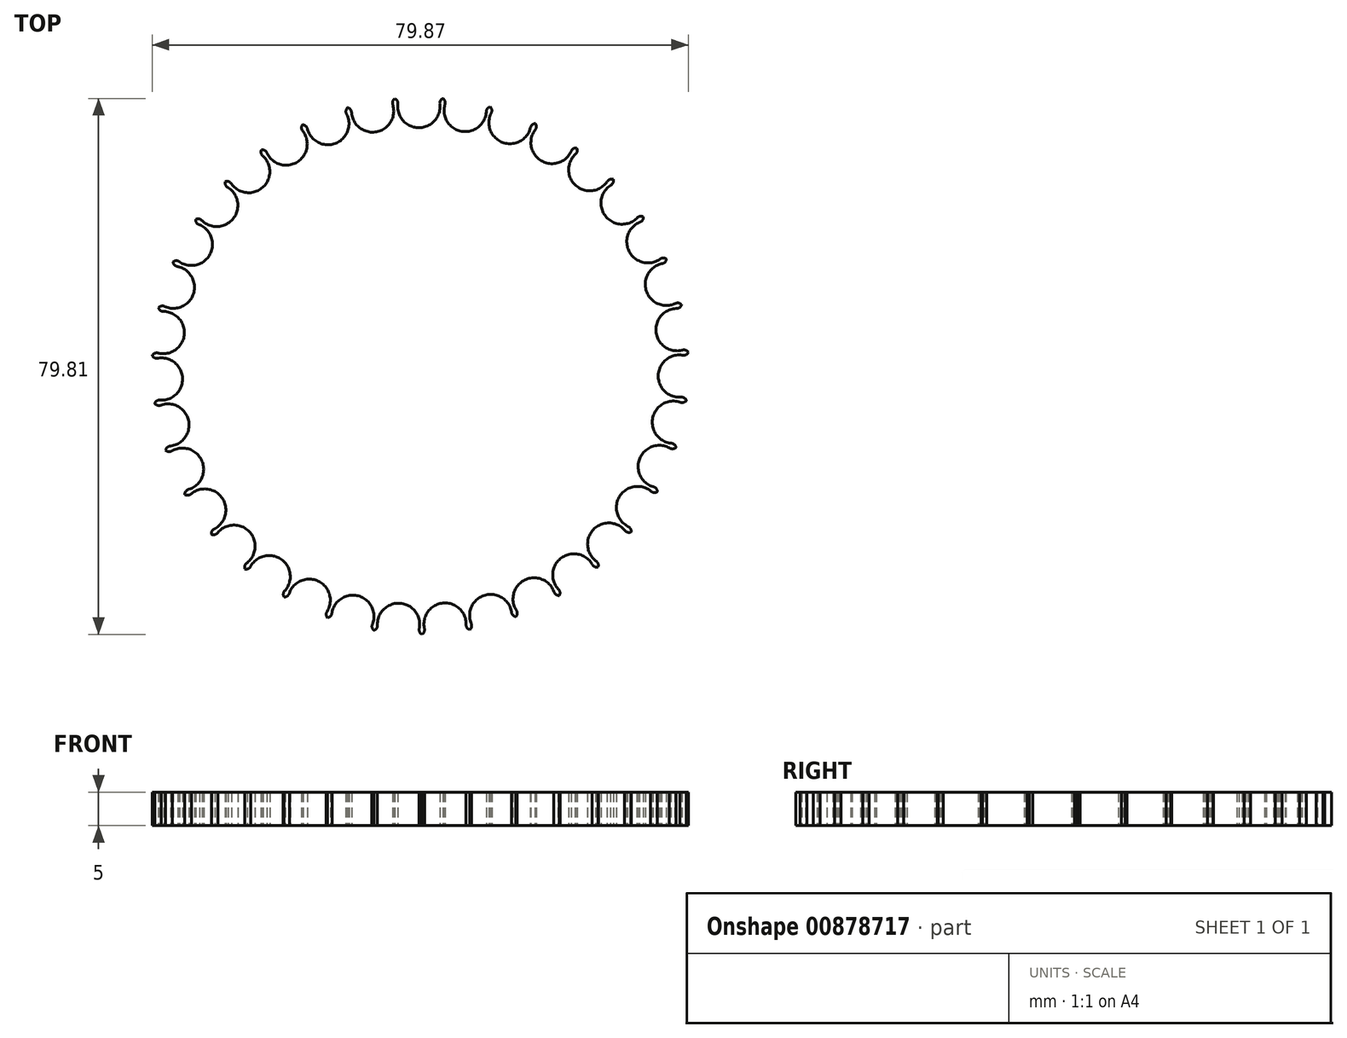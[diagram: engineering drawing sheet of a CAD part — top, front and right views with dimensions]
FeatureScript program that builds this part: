
annotation { "Feature Type Name" : "Feature", "Feature Type Description" : "" }
export const myFeature = defineFeature(function(context is Context, id is Id, definition is map)
    precondition{}
    {
        {
            var Q0;
            Q0=qCreatedBy(makeId("Top.planeOp"),FACE);
            var sketch = newSketch(context, id + "F0", { "sketchPlane" : qUnion([Q0])});
            skArc(sketch, "E0.0", {"start": v(-27.46, 84.28) * mm, "mid": v(-28.98, 79.88) * mm, "end": v(-24.46, 78.78) * mm});
            skArc(sketch, "E1.0", {"start": v(-31.8, 89.77) * mm, "mid": v(-32.52, 85.17) * mm, "end": v(-27.87, 84.9) * mm});
            skArc(sketch, "E2.0", {"start": v(-24.17, 78.1) * mm, "mid": v(-26.45, 74.05) * mm, "end": v(-22.2, 72.16) * mm});
            skArc(sketch, "E3.0", {"start": v(-22.03, 71.44) * mm, "mid": v(-25, 67.86) * mm, "end": v(-21.15, 65.23) * mm});
            skArc(sketch, "E4.0", {"start": v(-21.11, 64.5) * mm, "mid": v(-24.68, 61.5) * mm, "end": v(-21.36, 58.24) * mm});
            skArc(sketch, "E5.0", {"start": v(-21.45, 57.5) * mm, "mid": v(-25.5, 55.2) * mm, "end": v(-22.81, 51.39) * mm});
            skArc(sketch, "E6.0", {"start": v(-23.04, 50.7) * mm, "mid": v(-27.42, 49.14) * mm, "end": v(-25.47, 44.91) * mm});
            skArc(sketch, "E7.0", {"start": v(-25.81, 44.26) * mm, "mid": v(-30.4, 43.52) * mm, "end": v(-29.24, 39.01) * mm});
            skArc(sketch, "E8.0.0", {"start": v(-24.46, 78.78) * mm, "mid": v(-28.98, 79.88) * mm, "end": v(-27.46, 84.28) * mm});
            skArc(sketch, "E8.0.1", {"start": v(-27.46, 84.28) * mm, "mid": v(-27.01, 84.61) * mm, "end": v(-26.9, 85.16) * mm});
            skArc(sketch, "E8.0.3", {"start": v(-23.42, 78.78) * mm, "mid": v(-23.94, 78.98) * mm, "end": v(-24.46, 78.78) * mm});
            skArc(sketch, "E9.0", {"start": v(-29.69, 38.44) * mm, "mid": v(-34.34, 38.52) * mm, "end": v(-34, 33.88) * mm});
            skArc(sketch, "E10.0", {"start": v(-34.55, 33.4) * mm, "mid": v(-39.11, 34.31) * mm, "end": v(-39.6, 29.68) * mm});
            skArc(sketch, "E11.0", {"start": v(-40.22, 29.3) * mm, "mid": v(-44.55, 31.02) * mm, "end": v(-45.86, 26.55) * mm});
            skArc(sketch, "E12.0", {"start": v(-46.54, 26.29) * mm, "mid": v(-50.5, 28.75) * mm, "end": v(-52.58, 24.58) * mm});
            skArc(sketch, "E13.0", {"start": v(-53.3, 24.45) * mm, "mid": v(-56.75, 27.58) * mm, "end": v(-59.54, 23.85) * mm});
            skArc(sketch, "E14.0", {"start": v(-60.27, 23.85) * mm, "mid": v(-63.1, 27.54) * mm, "end": v(-66.52, 24.37) * mm});
            skArc(sketch, "E15.0", {"start": v(-67.24, 24.5) * mm, "mid": v(-69.37, 28.64) * mm, "end": v(-73.3, 26.13) * mm});
            skArc(sketch, "E16.0", {"start": v(-73.98, 26.39) * mm, "mid": v(-75.34, 30.84) * mm, "end": v(-79.65, 29.08) * mm});
            skArc(sketch, "E17.0", {"start": v(-80.28, 29.45) * mm, "mid": v(-80.82, 34.07) * mm, "end": v(-85.37, 33.1) * mm});
            skArc(sketch, "E18.0", {"start": v(-85.93, 33.58) * mm, "mid": v(-85.63, 38.23) * mm, "end": v(-90.29, 38.1) * mm});
            skArc(sketch, "E19.0", {"start": v(-90.75, 38.66) * mm, "mid": v(-89.63, 43.18) * mm, "end": v(-94.23, 43.87) * mm});
            skArc(sketch, "E20.0", {"start": v(-94.58, 44.52) * mm, "mid": v(-92.67, 48.76) * mm, "end": v(-97.08, 50.27) * mm});
            skArc(sketch, "E21.0", {"start": v(-97.3, 50.97) * mm, "mid": v(-94.67, 54.8) * mm, "end": v(-98.74, 57.07) * mm});
            skArc(sketch, "E22.0", {"start": v(-98.84, 57.8) * mm, "mid": v(-95.56, 61.1) * mm, "end": v(-99.16, 64.06) * mm});
            skArc(sketch, "E23.0", {"start": v(-99.13, 64.8) * mm, "mid": v(-95.31, 67.46) * mm, "end": v(-98.32, 71) * mm});
            skArc(sketch, "E24.0", {"start": v(-98.16, 71.72) * mm, "mid": v(-93.93, 73.67) * mm, "end": v(-96.26, 77.7) * mm});
            skArc(sketch, "E25.0", {"start": v(-95.98, 78.37) * mm, "mid": v(-91.46, 79.53) * mm, "end": v(-93.04, 83.91) * mm});
            skArc(sketch, "E26.0", {"start": v(-92.64, 84.53) * mm, "mid": v(-88, 84.86) * mm, "end": v(-88.75, 89.45) * mm});
            skArc(sketch, "E27.0", {"start": v(-88.25, 89.98) * mm, "mid": v(-83.62, 89.48) * mm, "end": v(-83.55, 94.13) * mm});
            skArc(sketch, "E28.0", {"start": v(-82.96, 94.57) * mm, "mid": v(-78.5, 93.25) * mm, "end": v(-77.6, 97.82) * mm});
            skArc(sketch, "E29.0", {"start": v(-76.94, 98.14) * mm, "mid": v(-72.78, 96.04) * mm, "end": v(-71.08, 100.37) * mm});
            skArc(sketch, "E30.0", {"start": v(-70.38, 100.57) * mm, "mid": v(-66.66, 97.77) * mm, "end": v(-64.21, 101.73) * mm});
            skPoint(sketch, "E31.0", {"position": v(-60.33, 98.37) * mm});
            skArc(sketch, "E32.0", {"start": v(-63.48, 101.8) * mm, "mid": v(-60.33, 98.37) * mm, "end": v(-57.21, 101.83) * mm});
            skArc(sketch, "E33.0", {"start": v(-56.48, 101.77) * mm, "mid": v(-54, 97.84) * mm, "end": v(-50.3, 100.69) * mm});
            skArc(sketch, "E34.0", {"start": v(-49.6, 100.5) * mm, "mid": v(-47.85, 96.18) * mm, "end": v(-43.72, 98.33) * mm});
            skArc(sketch, "E35.0", {"start": v(-43.06, 98.01) * mm, "mid": v(-42.1, 93.45) * mm, "end": v(-37.65, 94.83) * mm});
            skArc(sketch, "E36.0", {"start": v(-37.06, 94.4) * mm, "mid": v(-36.94, 89.74) * mm, "end": v(-32.31, 90.3) * mm});
            skPoint(sketch, "E37.0", {"position": v(-31.42, 90.18) * mm});
            skArc(sketch, "E38.0", {"start": v(-31.8, 89.77) * mm, "mid": v(-31.42, 90.18) * mm, "end": v(-31.4, 90.73) * mm});
            skArc(sketch, "E39.0", {"start": v(-32.31, 90.3) * mm, "mid": v(-31.9, 90.67) * mm, "end": v(-31.34, 90.67) * mm});
            skArc(sketch, "E40.0", {"start": v(-27.87, 84.9) * mm, "mid": v(-27.4, 85.18) * mm, "end": v(-26.84, 85.08) * mm});
            skArc(sketch, "E41.0", {"start": v(-24.17, 78.1) * mm, "mid": v(-23.67, 78.35) * mm, "end": v(-23.45, 78.87) * mm});
            skPoint(sketch, "E42.0", {"position": v(-21.65, 72.26) * mm});
            skArc(sketch, "E43.0", {"start": v(-22.2, 72.16) * mm, "mid": v(-21.65, 72.26) * mm, "end": v(-21.17, 71.97) * mm});
            skArc(sketch, "E44.0", {"start": v(-22.03, 71.44) * mm, "mid": v(-21.5, 71.6) * mm, "end": v(-21.2, 72.06) * mm});
            skPoint(sketch, "E45.0", {"position": v(-20.6, 65.24) * mm});
            skArc(sketch, "E46.0", {"start": v(-21.15, 65.23) * mm, "mid": v(-20.6, 65.24) * mm, "end": v(-20.18, 64.87) * mm});
            skArc(sketch, "E47.0", {"start": v(-21.11, 64.5) * mm, "mid": v(-20.56, 64.55) * mm, "end": v(-20.18, 64.96) * mm});
            skArc(sketch, "E48.0", {"start": v(-21.36, 58.24) * mm, "mid": v(-20.81, 58.14) * mm, "end": v(-20.47, 57.7) * mm});
            skArc(sketch, "E49.0", {"start": v(-21.45, 57.5) * mm, "mid": v(-20.9, 57.46) * mm, "end": v(-20.45, 57.8) * mm});
            skPoint(sketch, "E50.0", {"position": v(-22.3, 51.2) * mm});
            skArc(sketch, "E51.0", {"start": v(-22.81, 51.39) * mm, "mid": v(-22.3, 51.2) * mm, "end": v(-22.03, 50.7) * mm});
            skArc(sketch, "E52.0", {"start": v(-23.04, 50.7) * mm, "mid": v(-22.5, 50.54) * mm, "end": v(-22, 50.8) * mm});
            skArc(sketch, "E53.0", {"start": v(-25.47, 44.91) * mm, "mid": v(-24.99, 44.63) * mm, "end": v(-24.82, 44.1) * mm});
            skPoint(sketch, "E54.0", {"position": v(-25.3, 44.03) * mm});
            skArc(sketch, "E55.0", {"start": v(-25.81, 44.26) * mm, "mid": v(-25.3, 44.02) * mm, "end": v(-24.77, 44.18) * mm});
            skPoint(sketch, "E56.0", {"position": v(-28.82, 38.65) * mm});
            skArc(sketch, "E57.0", {"start": v(-29.24, 39.01) * mm, "mid": v(-28.81, 38.65) * mm, "end": v(-28.74, 38.1) * mm});
            skArc(sketch, "E58.0", {"start": v(-29.69, 38.44) * mm, "mid": v(-29.24, 38.11) * mm, "end": v(-28.68, 38.17) * mm});
            skArc(sketch, "E59.0", {"start": v(-34, 33.88) * mm, "mid": v(-33.65, 33.45) * mm, "end": v(-33.67, 32.9) * mm});
            skArc(sketch, "E60.0", {"start": v(-34.55, 33.4) * mm, "mid": v(-34.16, 33) * mm, "end": v(-33.6, 32.95) * mm});
            skPoint(sketch, "E61.0", {"position": v(-39.33, 29.2) * mm});
            skArc(sketch, "E62.0", {"start": v(-39.6, 29.68) * mm, "mid": v(-39.33, 29.2) * mm, "end": v(-39.46, 28.65) * mm});
            skPoint(sketch, "E63.0", {"position": v(-39.91, 28.84) * mm});
            skArc(sketch, "E64.0", {"start": v(-40.22, 29.3) * mm, "mid": v(-39.92, 28.84) * mm, "end": v(-39.38, 28.7) * mm});
            skArc(sketch, "E65.0", {"start": v(-45.86, 26.55) * mm, "mid": v(-45.68, 26.02) * mm, "end": v(-45.9, 25.5) * mm});
            skArc(sketch, "E66.0", {"start": v(-46.54, 26.29) * mm, "mid": v(-46.32, 25.78) * mm, "end": v(-45.82, 25.54) * mm});
            skArc(sketch, "E67.0", {"start": v(-52.58, 24.58) * mm, "mid": v(-52.5, 24.03) * mm, "end": v(-52.8, 23.57) * mm});
            skPoint(sketch, "E68.0", {"position": v(-53.17, 23.9) * mm});
            skArc(sketch, "E69.0", {"start": v(-53.3, 24.45) * mm, "mid": v(-53.17, 23.9) * mm, "end": v(-52.72, 23.59) * mm});
            skPoint(sketch, "E70.0", {"position": v(-59.56, 23.3) * mm});
            skArc(sketch, "E71.0", {"start": v(-59.54, 23.85) * mm, "mid": v(-59.56, 23.3) * mm, "end": v(-59.95, 22.9) * mm});
            skPoint(sketch, "E72.0", {"position": v(-60.24, 23.3) * mm});
            skArc(sketch, "E73.0", {"start": v(-60.27, 23.85) * mm, "mid": v(-60.24, 23.3) * mm, "end": v(-59.85, 22.9) * mm});
            skArc(sketch, "E74.0", {"start": v(-66.52, 24.37) * mm, "mid": v(-66.64, 23.83) * mm, "end": v(-67.1, 23.5) * mm});
            skArc(sketch, "E75.0", {"start": v(-67.24, 24.5) * mm, "mid": v(-67.31, 23.95) * mm, "end": v(-67, 23.49) * mm});
            skPoint(sketch, "E76.0", {"position": v(-73.51, 25.62) * mm});
            skArc(sketch, "E77.0", {"start": v(-73.3, 26.13) * mm, "mid": v(-73.5, 25.62) * mm, "end": v(-74.01, 25.38) * mm});
            skArc(sketch, "E78.0", {"start": v(-73.98, 26.39) * mm, "mid": v(-74.15, 25.86) * mm, "end": v(-73.93, 25.35) * mm});
            skPoint(sketch, "E79.0", {"position": v(-79.95, 28.61) * mm});
            skArc(sketch, "E80.0", {"start": v(-79.65, 29.08) * mm, "mid": v(-79.95, 28.6) * mm, "end": v(-80.49, 28.46) * mm});
            skArc(sketch, "E81.0", {"start": v(-80.28, 29.45) * mm, "mid": v(-80.54, 28.96) * mm, "end": v(-80.4, 28.42) * mm});
            skArc(sketch, "E82.0", {"start": v(-85.37, 33.1) * mm, "mid": v(-85.75, 32.7) * mm, "end": v(-86.3, 32.65) * mm});
            skArc(sketch, "E83.0", {"start": v(-85.93, 33.58) * mm, "mid": v(-86.27, 33.15) * mm, "end": v(-86.24, 32.6) * mm});
            skArc(sketch, "E84.0", {"start": v(-90.29, 38.1) * mm, "mid": v(-90.73, 37.76) * mm, "end": v(-91.29, 37.81) * mm});
            skArc(sketch, "E85.0", {"start": v(-90.75, 38.66) * mm, "mid": v(-91.16, 38.3) * mm, "end": v(-91.23, 37.74) * mm});
            skArc(sketch, "E86.0", {"start": v(-94.23, 43.87) * mm, "mid": v(-94.73, 43.63) * mm, "end": v(-95.26, 43.78) * mm});
            skArc(sketch, "E87.0", {"start": v(-94.58, 44.52) * mm, "mid": v(-95.06, 44.23) * mm, "end": v(-95.22, 43.7) * mm});
            skArc(sketch, "E88.0", {"start": v(-97.08, 50.27) * mm, "mid": v(-97.61, 50.12) * mm, "end": v(-98.11, 50.36) * mm});
            skArc(sketch, "E89.0", {"start": v(-97.3, 50.97) * mm, "mid": v(-97.83, 50.77) * mm, "end": v(-98.08, 50.27) * mm});
            skArc(sketch, "E90.0", {"start": v(-98.74, 57.07) * mm, "mid": v(-99.3, 57.02) * mm, "end": v(-99.74, 57.34) * mm});
            skArc(sketch, "E91.0", {"start": v(-98.84, 57.8) * mm, "mid": v(-99.39, 57.7) * mm, "end": v(-99.73, 57.25) * mm});
            skArc(sketch, "E92.0", {"start": v(-99.16, 64.06) * mm, "mid": v(-99.71, 64.1) * mm, "end": v(-100.1, 64.5) * mm});
            skPoint(sketch, "E93.0", {"position": v(-99.68, 64.79) * mm});
            skArc(sketch, "E94.0", {"start": v(-99.13, 64.8) * mm, "mid": v(-99.68, 64.79) * mm, "end": v(-100.1, 64.42) * mm});
            skPoint(sketch, "E95.0", {"position": v(-98.86, 71.15) * mm});
            skArc(sketch, "E96.0", {"start": v(-98.32, 71) * mm, "mid": v(-98.86, 71.15) * mm, "end": v(-99.16, 71.62) * mm});
            skArc(sketch, "E97.0", {"start": v(-98.16, 71.72) * mm, "mid": v(-98.71, 71.82) * mm, "end": v(-99.18, 71.53) * mm});
            skArc(sketch, "E98.0", {"start": v(-96.26, 77.7) * mm, "mid": v(-96.76, 77.94) * mm, "end": v(-96.98, 78.45) * mm});
            skArc(sketch, "E99.0", {"start": v(-95.98, 78.37) * mm, "mid": v(-96.5, 78.57) * mm, "end": v(-97.01, 78.36) * mm});
            skPoint(sketch, "E100.0", {"position": v(-93.49, 84.24) * mm});
            skArc(sketch, "E101.0", {"start": v(-92.64, 84.53) * mm, "mid": v(-93.11, 84.8) * mm, "end": v(-93.66, 84.7) * mm});
            skArc(sketch, "E102.0", {"start": v(-88.75, 89.45) * mm, "mid": v(-89.14, 89.85) * mm, "end": v(-89.16, 90.4) * mm});
            skArc(sketch, "E103.0", {"start": v(-88.25, 89.98) * mm, "mid": v(-88.67, 90.35) * mm, "end": v(-89.23, 90.34) * mm});
            skArc(sketch, "E104.0", {"start": v(-83.55, 94.13) * mm, "mid": v(-83.86, 94.6) * mm, "end": v(-83.79, 95.15) * mm});
            skArc(sketch, "E105.0", {"start": v(-82.96, 94.57) * mm, "mid": v(-83.3, 95) * mm, "end": v(-83.86, 95.1) * mm});
            skArc(sketch, "E106.0", {"start": v(-77.6, 97.82) * mm, "mid": v(-77.82, 98.32) * mm, "end": v(-77.65, 98.85) * mm});
            skArc(sketch, "E107.0", {"start": v(-76.94, 98.14) * mm, "mid": v(-77.2, 98.63) * mm, "end": v(-77.73, 98.81) * mm});
            skArc(sketch, "E108.0", {"start": v(-71.08, 100.37) * mm, "mid": v(-71.2, 100.91) * mm, "end": v(-70.94, 101.4) * mm});
            skArc(sketch, "E109.0", {"start": v(-70.38, 100.57) * mm, "mid": v(-70.55, 101.1) * mm, "end": v(-71.03, 101.38) * mm});
            skPoint(sketch, "E110.0", {"position": v(-64.24, 102.28) * mm});
            skArc(sketch, "E111.0", {"start": v(-63.48, 101.8) * mm, "mid": v(-63.56, 102.35) * mm, "end": v(-63.98, 102.7) * mm});
            skPoint(sketch, "E112.0", {"position": v(-57.14, 102.38) * mm});
            skArc(sketch, "E113.0", {"start": v(-57.21, 101.83) * mm, "mid": v(-57.14, 102.38) * mm, "end": v(-56.72, 102.75) * mm});
            skArc(sketch, "E114.0", {"start": v(-56.48, 101.77) * mm, "mid": v(-56.46, 102.33) * mm, "end": v(-56.81, 102.76) * mm});
            skArc(sketch, "E115.0", {"start": v(-50.3, 100.69) * mm, "mid": v(-50.14, 101.22) * mm, "end": v(-49.66, 101.5) * mm});
            skArc(sketch, "E116.0", {"start": v(-49.6, 100.5) * mm, "mid": v(-49.48, 101.04) * mm, "end": v(-49.75, 101.52) * mm});
            skPoint(sketch, "E117.0", {"position": v(-43.46, 98.82) * mm});
            skArc(sketch, "E118.0", {"start": v(-43.72, 98.33) * mm, "mid": v(-43.46, 98.82) * mm, "end": v(-42.94, 99.01) * mm});
            skArc(sketch, "E119.0", {"start": v(-43.06, 98.01) * mm, "mid": v(-42.84, 98.52) * mm, "end": v(-43.02, 99.05) * mm});
            skArc(sketch, "E120.0", {"start": v(-37.65, 94.83) * mm, "mid": v(-37.31, 95.26) * mm, "end": v(-36.76, 95.36) * mm});
            skArc(sketch, "E121.0", {"start": v(-37.06, 94.4) * mm, "mid": v(-36.75, 94.86) * mm, "end": v(-36.84, 95.41) * mm});
            skArc(sketch, "E122.0", {"start": v(-64.21, 101.73) * mm, "mid": v(-64.24, 102.28) * mm, "end": v(-63.9, 102.72) * mm});
            skArc(sketch, "E123.0", {"start": v(-93.04, 83.91) * mm, "mid": v(-93.49, 84.24) * mm, "end": v(-93.6, 84.78) * mm});
            skPoint(sketch, "E124.0", {"position": v(-60.13, 62.9) * mm});
            skSolve(sketch);
        }
        {
            var Q0;
            Q0 = qSketchRegion(id + "F0", true);
            extrude(context, id + "F1", {"entities" : qUnion([Q0]), "depth" : 5 * mm, "offsetDistance" : 25 * mm});
        }
    });
